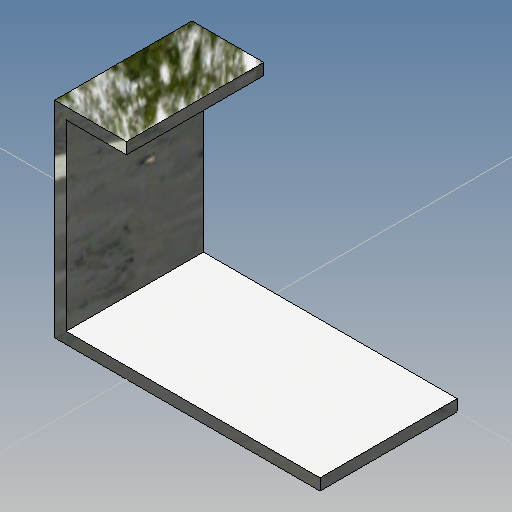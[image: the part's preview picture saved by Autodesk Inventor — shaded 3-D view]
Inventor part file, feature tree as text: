
AUTODESK INVENTOR PART (.ipt)
format: ipt  version: 2019 (Build 230136000, 136)  size: 166,400 bytes
history: native  units: in
note: dims shown in document units (in); Inventor stores cm internally (conversion verified against a paired STEP export)
features: extrude x2, sketch x2
ambient origin geometry x8: Origin, YZ Plane, XZ Plane, XY Plane, X Axis, Y Axis, Z Axis, Center Point
bodies: Solid1 (feature_tree)
feature tree (4):
  extrude  "Extrusion1"  Depth=0.12in TaperAngle=0.0deg
  extrude  "Extrusion2"  Depth=0.01in
  sketch  "Sketch1"  dims[d1=0.01in d2=0.12in d3=0.0in]
  sketch  "Sketch2"  dims[d4=0.222in d5=0.01in d6=0.12in d7=0.0in d8=0.18in]
